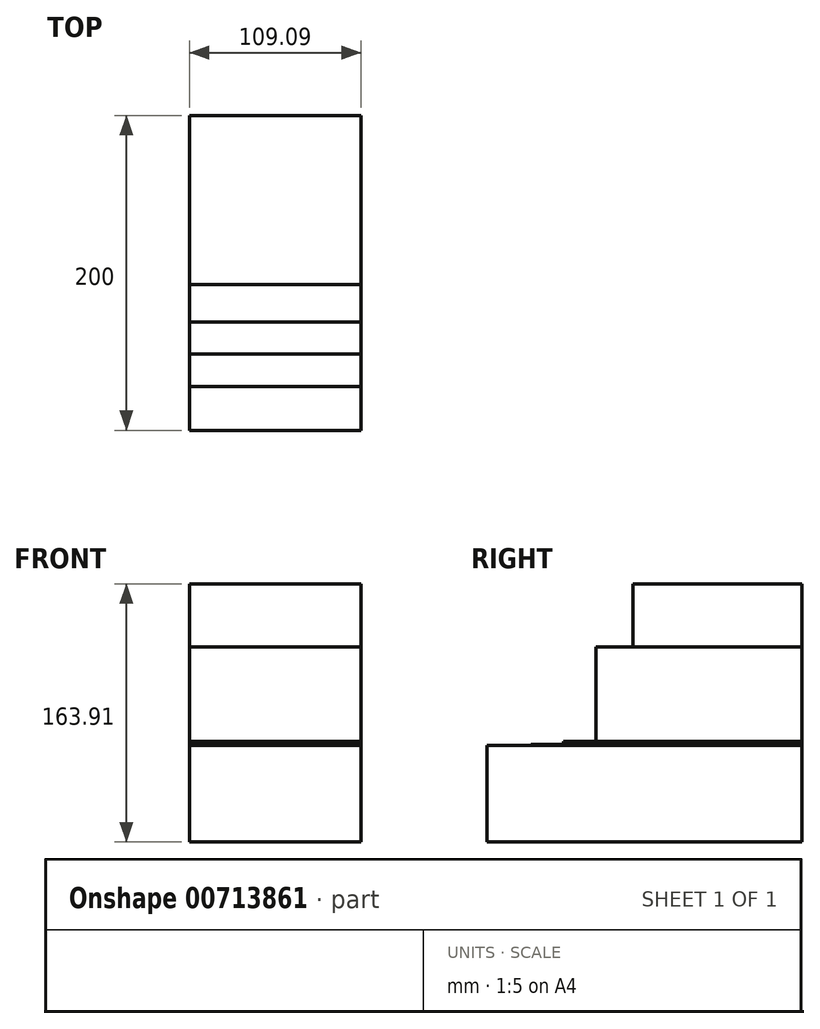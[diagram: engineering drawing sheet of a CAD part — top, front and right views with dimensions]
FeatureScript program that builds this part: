
annotation { "Feature Type Name" : "Feature", "Feature Type Description" : "" }
export const myFeature = defineFeature(function(context is Context, id is Id, definition is map)
    precondition{}
    {
        {
            var Q0;
            Q0=qCreatedBy(makeId("Front.planeOp"),FACE);
            var sketch = newSketch(context, id + "F0", { "sketchPlane" : qUnion([Q0])});
            skLineSegment(sketch, "E0.bottom", {"start": v(-49.45, 25.83) * mm, "end": v(59.64, 25.83) * mm});
            skLineSegment(sketch, "E0.top", {"start": v(-49.45, -35.58) * mm, "end": v(59.64, -35.58) * mm});
            skLineSegment(sketch, "E0.left", {"start": v(-49.45, 25.83) * mm, "end": v(-49.45, -35.58) * mm});
            skLineSegment(sketch, "E0.right", {"start": v(59.64, 25.83) * mm, "end": v(59.64, -35.58) * mm});
            skSolve(sketch);
        }
        {
            var Q0;
            Q0=makeQuery(id+"F0.imprint","IMPRINT",FACE,{"disambiguationData":[TD([[makeQuery(id+"F0.imprint","IMPRINT",EDGE,{"derivedFrom":sQuery(id+"F0.wireOp",EDGE,"E0.bottom")}),-1.0]])]});
            extrude(context, id + "F1", {"entities" : qUnion([Q0]), "depth" : 200 * mm});
        }
        {
            var Q0;
            Q0=makeQuery(id+"F1.opExtrude","SWEPT_FACE",FACE,{"disambiguationData":[OSD([sQuery(id+"F0.wireOp",EDGE,"E0.bottom")])]});
            var sketch = newSketch(context, id + "F2", { "sketchPlane" : qUnion([Q0])});
            skLineSegment(sketch, "E1.bottom", {"start": v(-49.45, 0) * mm, "end": v(59.64, 0) * mm});
            skLineSegment(sketch, "E1.top", {"start": v(-49.45, -172.22) * mm, "end": v(59.64, -172.22) * mm});
            skLineSegment(sketch, "E1.left", {"start": v(-49.45, 0) * mm, "end": v(-49.45, -172.22) * mm});
            skLineSegment(sketch, "E1.right", {"start": v(59.64, 0) * mm, "end": v(59.64, -172.22) * mm});
            skSolve(sketch);
        }
        {
            var Q0;
            Q0=makeQuery(id+"F2.imprint","IMPRINT",FACE,{"disambiguationData":[TD([[makeQuery(id+"F2.imprint","IMPRINT",EDGE,{"derivedFrom":sQuery(id+"F2.wireOp",EDGE,"E1.bottom")}),-1.0]])]});
            extrude(context, id + "F3", {"entities" : qUnion([Q0]), "depth" : 0.5 * mm});
        }
        {
            var Q0;
            Q0=makeQuery(id+"F3.opExtrude","CAP_FACE",FACE,{"disambiguationData":[OSD([sQuery(id+"F2.wireOp",EDGE,"E1.bottom"),sQuery(id+"F2.wireOp",EDGE,"E1.top"),sQuery(id+"F2.wireOp",EDGE,"E1.left"),sQuery(id+"F2.wireOp",EDGE,"E1.right")])],"isStart":false});
            var sketch = newSketch(context, id + "F4", { "sketchPlane" : qUnion([Q0])});
            skLineSegment(sketch, "E2.bottom", {"start": v(-49.45, 0) * mm, "end": v(59.64, 0) * mm});
            skLineSegment(sketch, "E2.top", {"start": v(-49.45, -151.4) * mm, "end": v(59.64, -151.4) * mm});
            skLineSegment(sketch, "E2.left", {"start": v(-49.45, 0) * mm, "end": v(-49.45, -151.4) * mm});
            skLineSegment(sketch, "E2.right", {"start": v(59.64, 0) * mm, "end": v(59.64, -151.4) * mm});
            skSolve(sketch);
        }
        {
            var Q0;
            Q0=makeQuery(id+"F4.imprint","IMPRINT",FACE,{"disambiguationData":[TD([[makeQuery(id+"F4.imprint","IMPRINT",EDGE,{"derivedFrom":sQuery(id+"F4.wireOp",EDGE,"E2.bottom")}),-1.0]])]});
            extrude(context, id + "F5", {"entities" : qUnion([Q0]), "depth" : 2 * mm});
        }
        {
            var Q0;
            Q0=makeQuery(id+"F5.opExtrude","CAP_FACE",FACE,{"disambiguationData":[OSD([sQuery(id+"F4.wireOp",EDGE,"E2.bottom"),sQuery(id+"F4.wireOp",EDGE,"E2.top"),sQuery(id+"F4.wireOp",EDGE,"E2.left"),sQuery(id+"F4.wireOp",EDGE,"E2.right")])],"isStart":false});
            var sketch = newSketch(context, id + "F6", { "sketchPlane" : qUnion([Q0])});
            skLineSegment(sketch, "E3.bottom", {"start": v(-49.45, 0) * mm, "end": v(59.64, 0) * mm});
            skLineSegment(sketch, "E3.top", {"start": v(-49.45, -131.03) * mm, "end": v(59.64, -131.03) * mm});
            skLineSegment(sketch, "E3.left", {"start": v(-49.45, 0) * mm, "end": v(-49.45, -131.03) * mm});
            skLineSegment(sketch, "E3.right", {"start": v(59.64, 0) * mm, "end": v(59.64, -131.03) * mm});
            skSolve(sketch);
        }
        {
            var Q0;
            Q0=makeQuery(id+"F6.imprint","IMPRINT",FACE,{"disambiguationData":[TD([[makeQuery(id+"F6.imprint","IMPRINT",EDGE,{"derivedFrom":sQuery(id+"F6.wireOp",EDGE,"E3.bottom")}),-1.0]])]});
            extrude(context, id + "F7", {"entities" : qUnion([Q0]), "depth" : 60 * mm});
        }
        {
            var Q0;
            Q0=makeQuery(id+"F7.opExtrude","CAP_FACE",FACE,{"disambiguationData":[OSD([sQuery(id+"F6.wireOp",EDGE,"E3.bottom"),sQuery(id+"F6.wireOp",EDGE,"E3.top"),sQuery(id+"F6.wireOp",EDGE,"E3.left"),sQuery(id+"F6.wireOp",EDGE,"E3.right")])],"isStart":false});
            var sketch = newSketch(context, id + "F8", { "sketchPlane" : qUnion([Q0])});
            skLineSegment(sketch, "E4.bottom", {"start": v(-49.45, 0) * mm, "end": v(59.64, 0) * mm});
            skLineSegment(sketch, "E4.top", {"start": v(-49.45, -107.35) * mm, "end": v(59.64, -107.35) * mm});
            skLineSegment(sketch, "E4.left", {"start": v(-49.45, 0) * mm, "end": v(-49.45, -107.35) * mm});
            skLineSegment(sketch, "E4.right", {"start": v(59.64, 0) * mm, "end": v(59.64, -107.35) * mm});
            skSolve(sketch);
        }
        {
            var Q0;
            Q0=makeQuery(id+"F8.imprint","IMPRINT",FACE,{"disambiguationData":[TD([[makeQuery(id+"F8.imprint","IMPRINT",EDGE,{"derivedFrom":sQuery(id+"F8.wireOp",EDGE,"E4.bottom")}),-1.0]])]});
            extrude(context, id + "F9", {"entities" : qUnion([Q0]), "depth" : 40 * mm});
        }
    });
